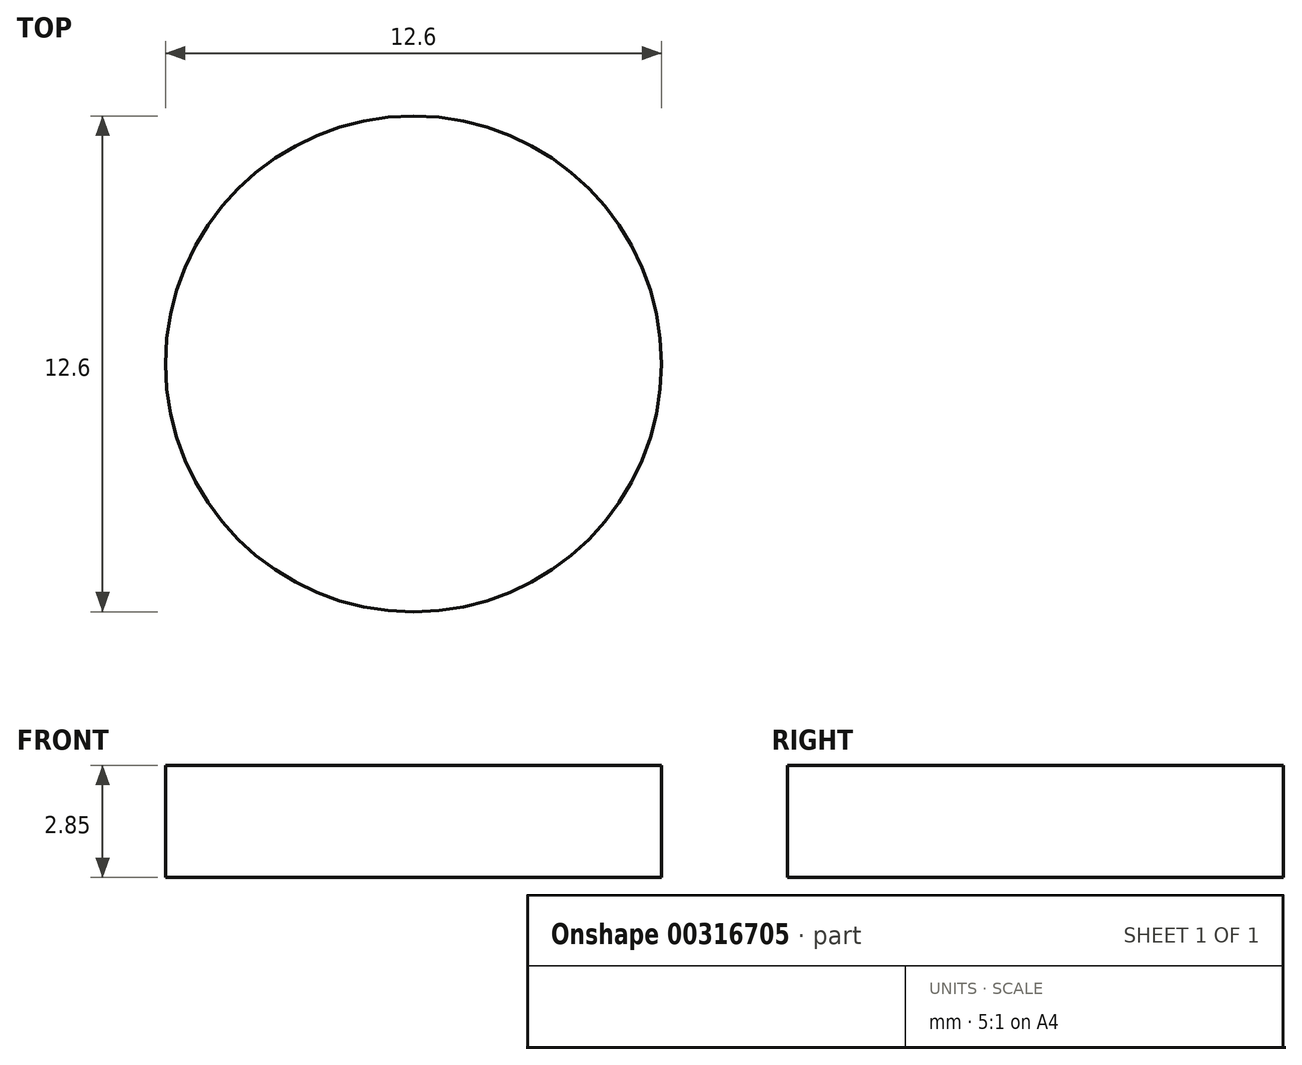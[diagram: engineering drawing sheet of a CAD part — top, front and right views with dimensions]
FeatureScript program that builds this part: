
annotation { "Feature Type Name" : "Feature", "Feature Type Description" : "" }
export const myFeature = defineFeature(function(context is Context, id is Id, definition is map)
    precondition{}
    {
        {
            var Q0;
            Q0=qCreatedBy(makeId("Top.planeOp"),FACE);
            var sketch = newSketch(context, id + "F0", { "sketchPlane" : qUnion([Q0])});
            skCircle(sketch, "E0", {"center": v(0, 0) * mm, "radius": 6.3 * mm});
            skSolve(sketch);
        }
        {
            var Q0;
            Q0=makeQuery(id+"F0.imprint","IMPRINT",FACE,{"disambiguationData":[TD([[makeQuery(id+"F0.imprint","IMPRINT",EDGE,{"derivedFrom":sQuery(id+"F0.wireOp",EDGE,"E0")}),1.0]])]});
            extrude(context, id + "F1", {"entities" : qUnion([Q0]), "depth" : 2.85 * mm});
        }
    });
